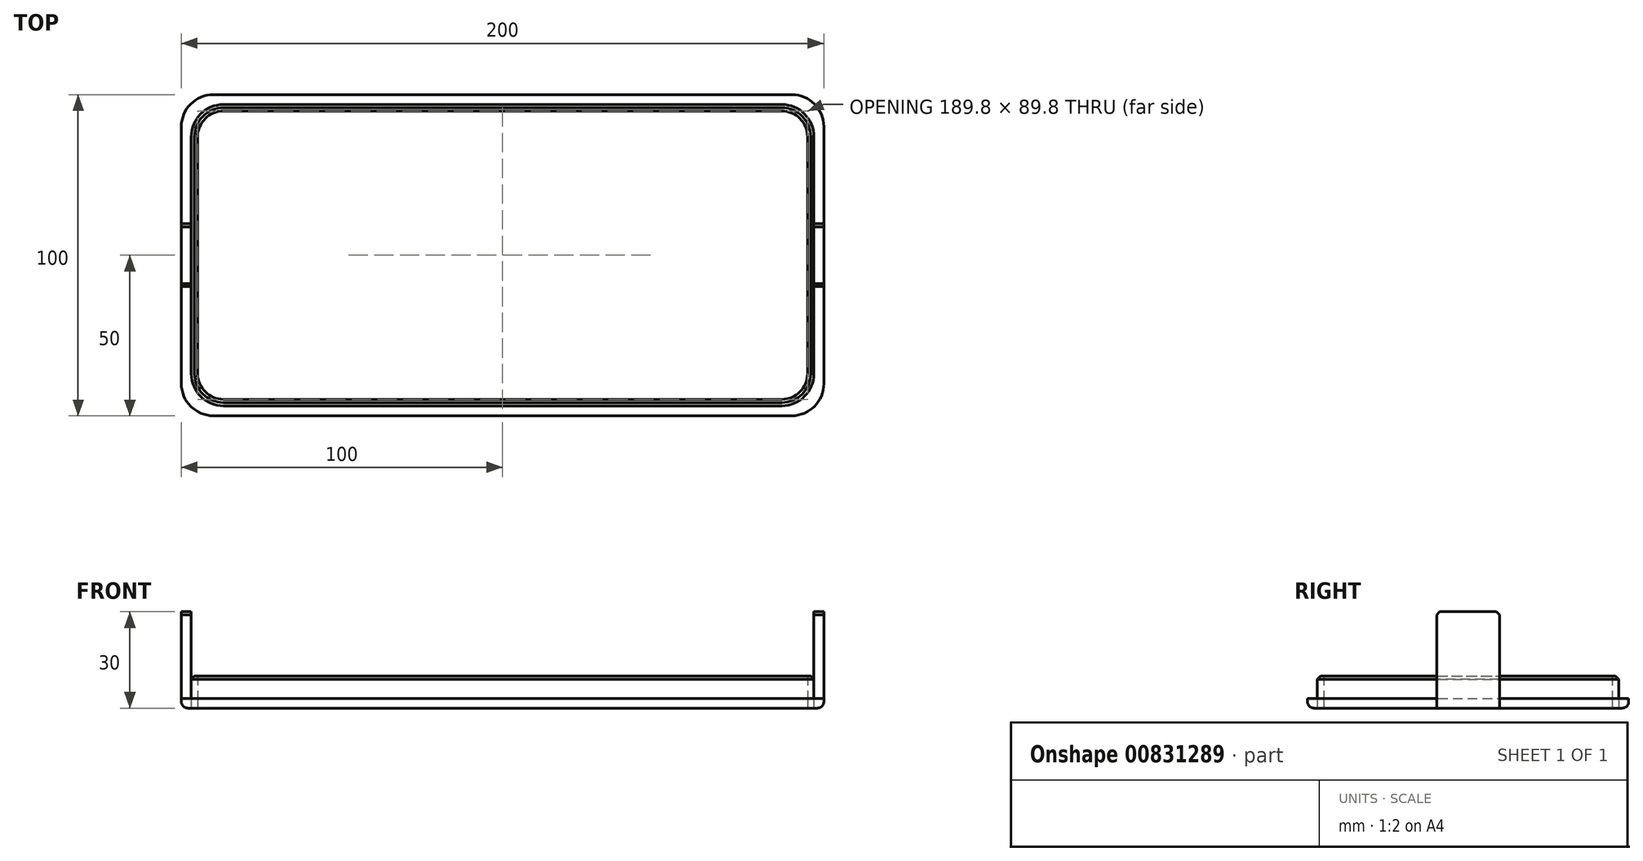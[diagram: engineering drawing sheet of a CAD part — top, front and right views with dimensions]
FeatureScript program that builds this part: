
annotation { "Feature Type Name" : "Feature", "Feature Type Description" : "" }
export const myFeature = defineFeature(function(context is Context, id is Id, definition is map)
    precondition{}
    {
        {
            var Q0;
            Q0=qCreatedBy(makeId("Top.planeOp"),FACE);
            var sketch = newSketch(context, id + "F0", { "sketchPlane" : qUnion([Q0])});
            skLineSegment(sketch, "E0.bottom", {"start": v(86.8, -46.9) * mm, "end": v(-87, -46.9) * mm});
            skLineSegment(sketch, "E0.top", {"start": v(86.8, 46.9) * mm, "end": v(-87, 46.9) * mm});
            skLineSegment(sketch, "E0.left", {"start": v(96.8, -36.9) * mm, "end": v(96.8, 36.9) * mm});
            skLineSegment(sketch, "E0.right", {"start": v(-97, -36.9) * mm, "end": v(-97, 36.9) * mm});
            skPoint(sketch, "E0.middle", {"position": v(-0.1, 0) * mm});
            skLineSegment(sketch, "E1.0", {"start": v(89.9, 50) * mm, "end": v(-90.1, 50) * mm});
            skLineSegment(sketch, "E1.1", {"start": v(99.9, -40) * mm, "end": v(99.9, 40) * mm});
            skLineSegment(sketch, "E1.2", {"start": v(89.9, -50) * mm, "end": v(-90.1, -50) * mm});
            skLineSegment(sketch, "E1.3", {"start": v(-100.1, -40) * mm, "end": v(-100.1, 40) * mm});
            skLineSegment(sketch, "E2", {"start": v(-97, -9.8) * mm, "end": v(-100.1, -9.8) * mm});
            skLineSegment(sketch, "E3", {"start": v(-97, 9.8) * mm, "end": v(-100.1, 9.8) * mm});
            skLineSegment(sketch, "E4", {"start": v(96.8, -9.8) * mm, "end": v(99.9, -9.8) * mm});
            skLineSegment(sketch, "E5", {"start": v(96.8, 9.8) * mm, "end": v(99.9, 9.8) * mm});
            skPoint(sketch, "E6.visualSharp", {"position": v(-97, 46.9) * mm});
            skArc(sketch, "E6.filletArc", {"start": v(-87, 46.9) * mm, "mid": v(-94.07, 43.97) * mm, "end": v(-97, 36.9) * mm});
            skPoint(sketch, "E7.visualSharp", {"position": v(-100.1, 50) * mm});
            skArc(sketch, "E7.filletArc", {"start": v(-90.1, 50) * mm, "mid": v(-97.17, 47.07) * mm, "end": v(-100.1, 40) * mm});
            skPoint(sketch, "E8.visualSharp", {"position": v(-97, -46.9) * mm});
            skArc(sketch, "E8.filletArc", {"start": v(-97, -36.9) * mm, "mid": v(-94.07, -43.97) * mm, "end": v(-87, -46.9) * mm});
            skPoint(sketch, "E9.visualSharp", {"position": v(-100.1, -50) * mm});
            skArc(sketch, "E9.filletArc", {"start": v(-100.1, -40) * mm, "mid": v(-97.17, -47.07) * mm, "end": v(-90.1, -50) * mm});
            skPoint(sketch, "E10.visualSharp", {"position": v(96.8, -46.9) * mm});
            skArc(sketch, "E10.filletArc", {"start": v(86.8, -46.9) * mm, "mid": v(93.87, -43.97) * mm, "end": v(96.8, -36.9) * mm});
            skPoint(sketch, "E11.visualSharp", {"position": v(99.9, -50) * mm});
            skArc(sketch, "E11.filletArc", {"start": v(89.9, -50) * mm, "mid": v(96.97, -47.07) * mm, "end": v(99.9, -40) * mm});
            skPoint(sketch, "E12.visualSharp", {"position": v(96.8, 46.9) * mm});
            skArc(sketch, "E12.filletArc", {"start": v(96.8, 36.9) * mm, "mid": v(93.87, 43.97) * mm, "end": v(86.8, 46.9) * mm});
            skPoint(sketch, "E13.visualSharp", {"position": v(99.9, 50) * mm});
            skArc(sketch, "E13.filletArc", {"start": v(99.9, 40) * mm, "mid": v(96.97, 47.07) * mm, "end": v(89.9, 50) * mm});
            skLineSegment(sketch, "E14.0", {"start": v(86.8, 44.9) * mm, "end": v(-87, 44.9) * mm});
            skArc(sketch, "E14.1", {"start": v(94.8, 36.9) * mm, "mid": v(92.46, 42.56) * mm, "end": v(86.8, 44.9) * mm});
            skArc(sketch, "E14.2", {"start": v(-87, 44.9) * mm, "mid": v(-92.66, 42.56) * mm, "end": v(-95, 36.9) * mm});
            skLineSegment(sketch, "E14.3", {"start": v(94.8, -36.9) * mm, "end": v(94.8, 36.9) * mm});
            skLineSegment(sketch, "E14.4", {"start": v(-95, -36.9) * mm, "end": v(-95, 36.9) * mm});
            skArc(sketch, "E14.5", {"start": v(-95, -36.9) * mm, "mid": v(-92.66, -42.56) * mm, "end": v(-87, -44.9) * mm});
            skLineSegment(sketch, "E14.6", {"start": v(86.8, -44.9) * mm, "end": v(-87, -44.9) * mm});
            skArc(sketch, "E14.7", {"start": v(86.8, -44.9) * mm, "mid": v(92.46, -42.56) * mm, "end": v(94.8, -36.9) * mm});
            skSolve(sketch);
        }
        {
            var Q0;
            Q0=makeQuery(id+"F0.imprint","IMPRINT",FACE,{"disambiguationData":[TD([[makeQuery(id+"F0.imprint","IMPRINT",EDGE,{"derivedFrom":sQuery(id+"F0.wireOp",EDGE,"E0.top")}),-1.0]])]});
            var Q1;
            Q1=makeQuery(id+"F0.imprint","IMPRINT",FACE,{"disambiguationData":[TD([[makeQuery(id+"F0.imprint","IMPRINT",EDGE,{"derivedFrom":sQuery(id+"F0.wireOp",EDGE,"E14.0")}),1.0]])]});
            var Q2;
            Q2=makeQuery(id+"F0.imprint","IMPRINT",FACE,{"disambiguationData":[TD([[makeQuery(id+"F0.imprint","IMPRINT",EDGE,{"derivedFrom":sQuery(id+"F0.wireOp",EDGE,"E0.bottom")}),1.0]])]});
            extrude(context, id + "F1", {"entities" : qUnion([Q0, Q1, Q2]), "depth" : 3 * mm, "offsetDistance" : 25 * mm});
        }
        {
            var Q0;
            Q0=makeQuery(id+"F0.imprint","IMPRINT",FACE,{"disambiguationData":[TD([[makeQuery(id+"F0.imprint","IMPRINT",EDGE,{"derivedFrom":sQuery(id+"F0.wireOp",EDGE,"E0.bottom")}),-1.0]])]});
            extrude(context, id + "F2", {"entities" : qUnion([Q0]), "depth" : 10 * mm, "offsetDistance" : 25 * mm});
        }
        {
            var Q0;
            {var subQ0=sQuery(id+"F0.wireOp",EDGE,"E2");Q0=makeQuery(id+"F0.imprint","IMPRINT",FACE,{"disambiguationData":[TD([[makeQuery(id+"F0.imprint","IMPRINT",EDGE,{"derivedFrom":subQ0}),-1.0]])]});}
            var Q1;
            {var subQ0=sQuery(id+"F0.wireOp",EDGE,"E4");Q1=makeQuery(id+"F0.imprint","IMPRINT",FACE,{"disambiguationData":[TD([[makeQuery(id+"F0.imprint","IMPRINT",EDGE,{"derivedFrom":subQ0}),1.0]])]});}
            extrude(context, id + "F3", {"entities" : qUnion([Q0, Q1]), "depth" : 30 * mm, "offsetDistance" : 25 * mm});
        }
        {
            var Q0;
            Q0=makeQuery(id+"F3.opExtrude","CAP_EDGE",EDGE,{"disambiguationData":[OSD([sQuery(id+"F0.wireOp",EDGE,"E2")])],"isStart":false});
            var Q1;
            Q1=makeQuery(id+"F3.opExtrude","CAP_EDGE",EDGE,{"disambiguationData":[OSD([sQuery(id+"F0.wireOp",EDGE,"E3")])],"isStart":false});
            var Q2;
            Q2=makeQuery(id+"F3.opExtrude","CAP_EDGE",EDGE,{"disambiguationData":[OSD([sQuery(id+"F0.wireOp",EDGE,"E5")])],"isStart":false});
            var Q3;
            Q3=makeQuery(id+"F3.opExtrude","CAP_EDGE",EDGE,{"disambiguationData":[OSD([sQuery(id+"F0.wireOp",EDGE,"E4")])],"isStart":false});
            var Q4;
            Q4=makeQuery(id+"F2.opExtrude","CAP_EDGE",EDGE,{"disambiguationData":[OSD([sQuery(id+"F0.wireOp",EDGE,"E0.left")])],"isStart":false});
            chamfer(context, id + "F4", {"entities" : qUnion([Q0, Q1, Q2, Q3, Q4]), "width" : 1 * mm, "tangentPropagation" : true});
        }
        {
            var Q0;
            {var subQ0=sQuery(id+"F0.wireOp",EDGE,"E1.1");Q0=makeQuery(id+"F1.opExtrude","CAP_EDGE",EDGE,{"disambiguationData":[OSD([subQ0]),TDD([makeQuery(id+"F0.imprint","IMPRINT",EDGE,{"disambiguationData":[TD([[makeQuery(id+"F0.imprint","INTERSECT",VERTEX,{"derivedFrom":[subQ0,sQuery(id+"F0.wireOp",EDGE,"E11.filletArc")]}),-1.0]])],"derivedFrom":subQ0})])],"isStart":true});}
            var Q1;
            Q1=makeQuery(id+"F3.opExtrude","CAP_EDGE",EDGE,{"disambiguationData":[OSD([sQuery(id+"F0.wireOp",EDGE,"E1.1")])],"isStart":true});
            var Q2;
            {var subQ0=sQuery(id+"F0.wireOp",EDGE,"E1.1");Q2=makeQuery(id+"F1.opExtrude","CAP_EDGE",EDGE,{"disambiguationData":[OSD([subQ0]),TDD([makeQuery(id+"F0.imprint","IMPRINT",EDGE,{"disambiguationData":[TD([[makeQuery(id+"F0.imprint","INTERSECT",VERTEX,{"derivedFrom":[subQ0,sQuery(id+"F0.wireOp",EDGE,"E13.filletArc")]}),1.0]])],"derivedFrom":subQ0})])],"isStart":true});}
            var Q3;
            Q3=makeQuery(id+"F3.opExtrude","CAP_EDGE",EDGE,{"disambiguationData":[OSD([sQuery(id+"F0.wireOp",EDGE,"E1.3")])],"isStart":true});
            fillet(context, id + "F5", {"entities" : qUnion([Q0, Q1, Q2, Q3]), "radius" : 2 * mm, "tangentPropagation" : true, "allowEdgeOverflow" : false});
        }
    });
